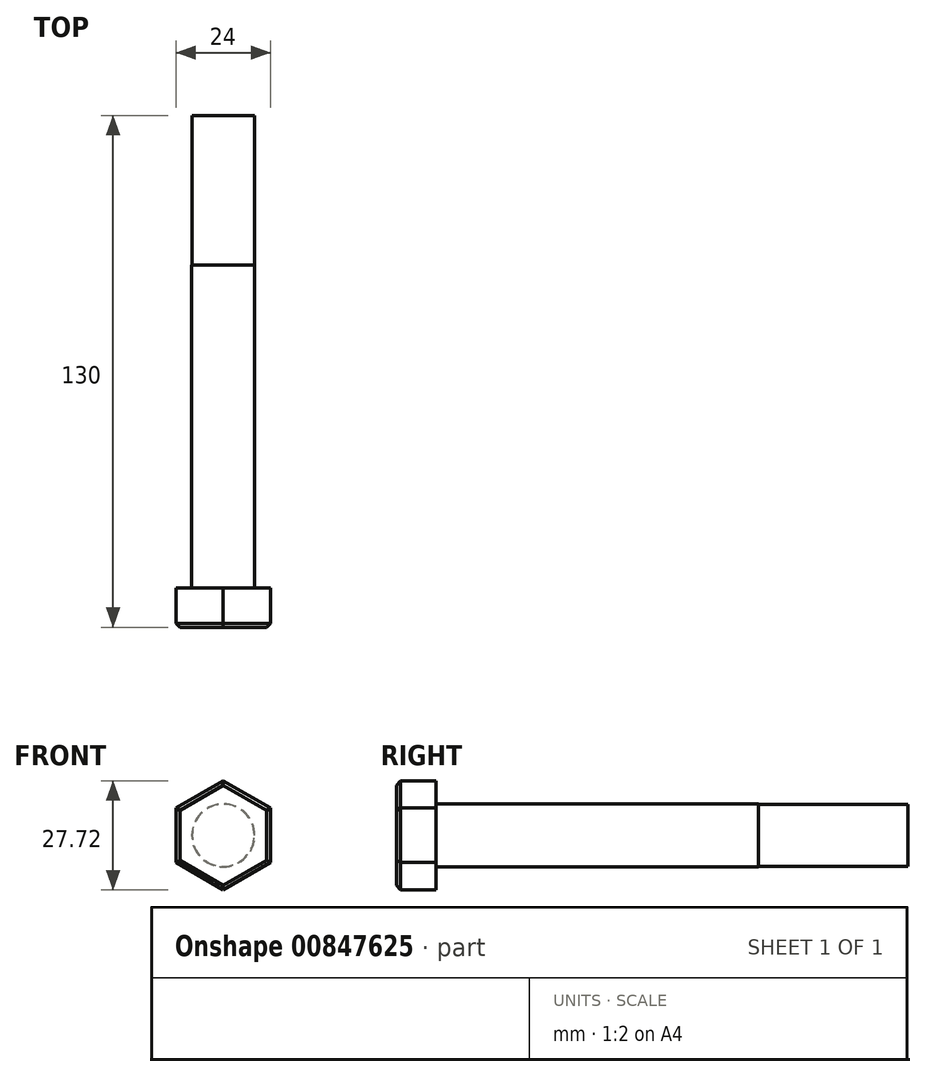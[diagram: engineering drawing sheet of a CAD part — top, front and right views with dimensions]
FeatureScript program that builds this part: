
annotation { "Feature Type Name" : "Feature", "Feature Type Description" : "" }
export const myFeature = defineFeature(function(context is Context, id is Id, definition is map)
    precondition{}
    {
        {
            var Q0;
            Q0=qCreatedBy(makeId("Front.planeOp"),FACE);
            var sketch = newSketch(context, id + "F0", { "sketchPlane" : qUnion([Q0])});
            skLineSegment(sketch, "E0", {"start": v(0, 45.9) * mm, "end": v(0, -43.11) * mm, "construction": true});
            skLineSegment(sketch, "E1", {"start": v(-56.15, 0) * mm, "end": v(55.88, 0) * mm, "construction": true});
            skCircle(sketch, "E2.cCircle", {"center": v(0, 0) * mm, "radius": 12 * mm, "construction": true});
            skLineSegment(sketch, "E2.0", {"start": v(12, -6.93) * mm, "end": v(0, -13.86) * mm});
            skLineSegment(sketch, "E2.1", {"start": v(0, -13.86) * mm, "end": v(-12, -6.93) * mm});
            skLineSegment(sketch, "E2.2", {"start": v(-12, -6.93) * mm, "end": v(-12, 6.93) * mm});
            skLineSegment(sketch, "E2.3", {"start": v(-12, 6.93) * mm, "end": v(0, 13.86) * mm});
            skLineSegment(sketch, "E2.4", {"start": v(0, 13.86) * mm, "end": v(12, 6.93) * mm});
            skLineSegment(sketch, "E2.5", {"start": v(12, 6.93) * mm, "end": v(12, -6.93) * mm});
            skPoint(sketch, "E2.0.midPoint", {"position": v(6, -10.4) * mm});
            skSolve(sketch);
        }
        {
            var Q0;
            Q0 = qSketchRegion(id + "F0", true);
            extrude(context, id + "F1", {"entities" : qUnion([Q0]), "depth" : 10 * mm, "offsetDistance" : 25 * mm});
        }
        {
            var Q0;
            Q0=makeQuery(id+"F1.opExtrude","CAP_EDGE",EDGE,{"disambiguationData":[OSD([sQuery(id+"F0.wireOp",EDGE,"E2.4")])],"isStart":false});
            var Q1;
            Q1=makeQuery(id+"F1.opExtrude","CAP_EDGE",EDGE,{"disambiguationData":[OSD([sQuery(id+"F0.wireOp",EDGE,"E2.3")])],"isStart":false});
            var Q2;
            Q2=makeQuery(id+"F1.opExtrude","CAP_EDGE",EDGE,{"disambiguationData":[OSD([sQuery(id+"F0.wireOp",EDGE,"E2.5")])],"isStart":false});
            var Q3;
            Q3=makeQuery(id+"F1.opExtrude","CAP_EDGE",EDGE,{"disambiguationData":[OSD([sQuery(id+"F0.wireOp",EDGE,"E2.0")])],"isStart":false});
            var Q4;
            Q4=makeQuery(id+"F1.opExtrude","CAP_EDGE",EDGE,{"disambiguationData":[OSD([sQuery(id+"F0.wireOp",EDGE,"E2.1")])],"isStart":false});
            var Q5;
            Q5=makeQuery(id+"F1.opExtrude","CAP_EDGE",EDGE,{"disambiguationData":[OSD([sQuery(id+"F0.wireOp",EDGE,"E2.2")])],"isStart":false});
            chamfer(context, id + "F2", {"entities" : qUnion([Q0, Q1, Q2, Q3, Q4, Q5]), "chamferType" : ChamferType.OFFSET_ANGLE, "width" : 1 * mm, "oppositeDirection" : false, "angle" : 45 * degree, "tangentPropagation" : true});
        }
        {
            var Q0;
            Q0=makeQuery(id+"F1.opExtrude","CAP_FACE",FACE,{"disambiguationData":[OSD([sQuery(id+"F0.wireOp",EDGE,"E2.0"),sQuery(id+"F0.wireOp",EDGE,"E2.1"),sQuery(id+"F0.wireOp",EDGE,"E2.2"),sQuery(id+"F0.wireOp",EDGE,"E2.3"),sQuery(id+"F0.wireOp",EDGE,"E2.4"),sQuery(id+"F0.wireOp",EDGE,"E2.5")])],"isStart":true});
            var sketch = newSketch(context, id + "F3", { "sketchPlane" : qUnion([Q0])});
            skCircle(sketch, "E3", {"center": v(0, 0) * mm, "radius": 8 * mm});
            skSolve(sketch);
        }
        {
            var Q0;
            Q0 = qSketchRegion(id + "F3", true);
            extrude(context, id + "F4", {"entities" : qUnion([Q0]), "operationType" : NewBodyOperationType.ADD, "depth" : 120 * mm, "offsetDistance" : 25 * mm});
        }
        {
            var Q0;
            Q0=makeQuery(id+"F4.opExtrude","CAP_FACE",FACE,{"disambiguationData":[OSD([sQuery(id+"F3.wireOp",EDGE,"E3")])],"isStart":false});
            var sketch = newSketch(context, id + "F5", { "sketchPlane" : qUnion([Q0])});
            skCircle(sketch, "E4.0", {"center": v(0, 0) * mm, "radius": 7.9 * mm});
            skCircle(sketch, "E5.0", {"center": v(0, 0) * mm, "radius": 8 * mm});
            skSolve(sketch);
        }
        {
            var Q0;
            Q0 = qSketchRegion(id + "F5", true);
            extrude(context, id + "F6", {"entities" : qUnion([Q0]), "operationType" : NewBodyOperationType.REMOVE, "oppositeDirection" : true, "depth" : 38 * mm, "offsetDistance" : 25 * mm});
        }
    });
